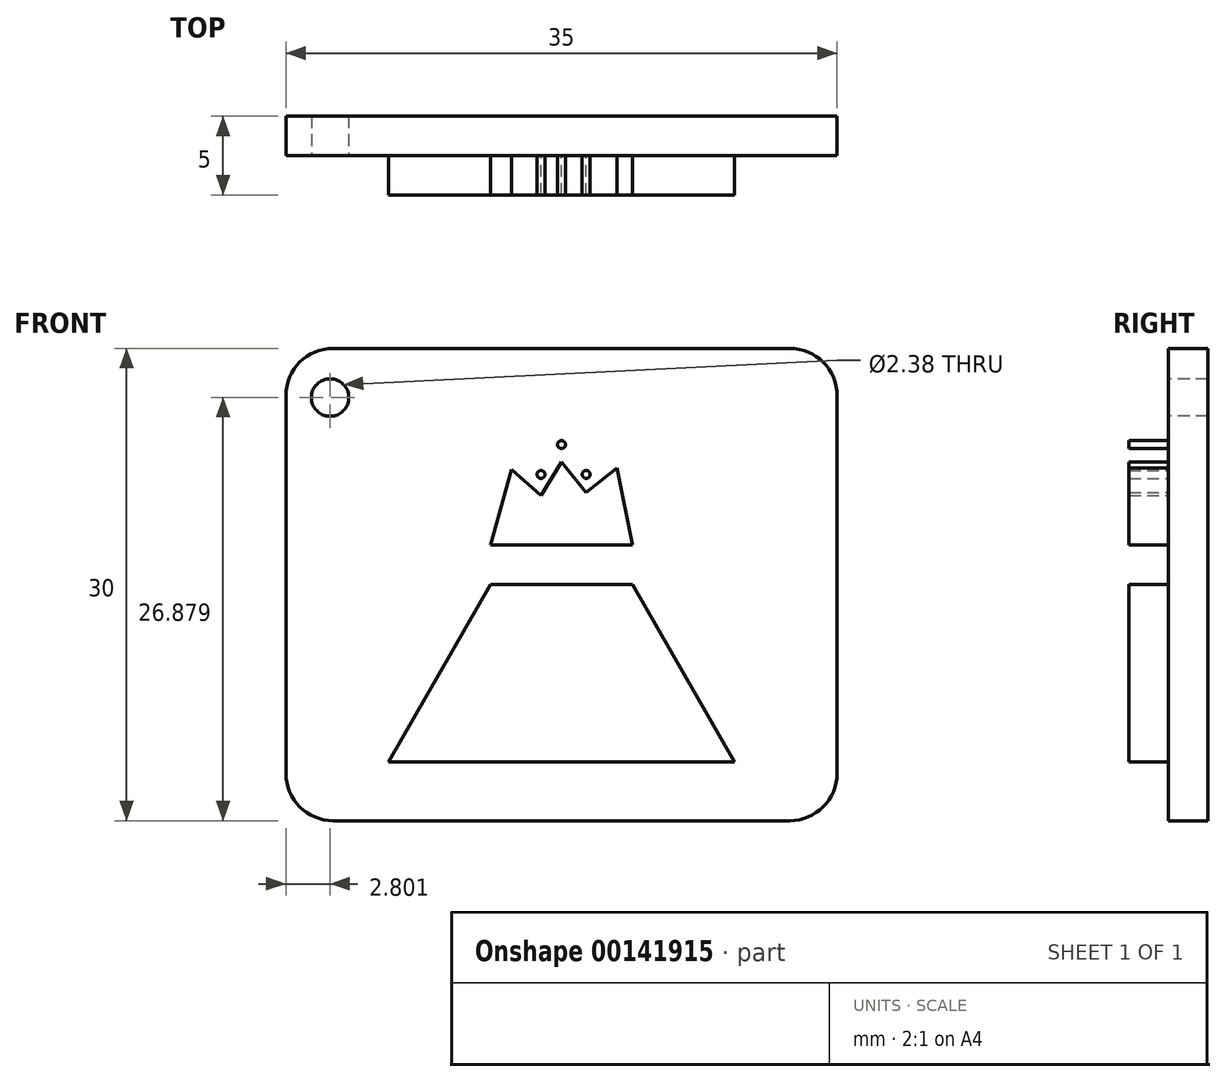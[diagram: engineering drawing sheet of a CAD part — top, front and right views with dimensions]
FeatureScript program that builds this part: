
annotation { "Feature Type Name" : "Feature", "Feature Type Description" : "" }
export const myFeature = defineFeature(function(context is Context, id is Id, definition is map)
    precondition{}
    {
        {
            var Q0;
            Q0=qCreatedBy(makeId("Front.planeOp"),FACE);
            var sketch = newSketch(context, id + "F0", { "sketchPlane" : qUnion([Q0])});
            skLineSegment(sketch, "E0.bottom", {"start": v(17.5, -15) * mm, "end": v(-17.5, -15) * mm});
            skLineSegment(sketch, "E0.top", {"start": v(17.5, 15) * mm, "end": v(-17.5, 15) * mm});
            skLineSegment(sketch, "E0.left", {"start": v(17.5, -15) * mm, "end": v(17.5, 15) * mm});
            skLineSegment(sketch, "E0.right", {"start": v(-17.5, -15) * mm, "end": v(-17.5, 15) * mm});
            skPoint(sketch, "E0.middle", {"position": v(0, 0) * mm});
            skCircle(sketch, "E1", {"center": v(-14.7, 11.88) * mm, "radius": 1.19 * mm});
            skSolve(sketch);
        }
        {
            var Q0;
            Q0 = qSketchRegion(id + "F0", true);
            extrude(context, id + "F1", {"entities" : qUnion([Q0]), "oppositeDirection" : true, "depth" : 2.5 * mm});
        }
        {
            var Q0;
            Q0=qCreatedBy(makeId("Front.planeOp"),FACE);
            var sketch = newSketch(context, id + "F2", { "sketchPlane" : qUnion([Q0])});
            skLineSegment(sketch, "E2", {"start": v(-11, -11.26) * mm, "end": v(11, -11.26) * mm});
            skLineSegment(sketch, "E3", {"start": v(0, -11.26) * mm, "end": v(0, 0) * mm, "construction": true});
            skLineSegment(sketch, "E4", {"start": v(4.5, 0) * mm, "end": v(-4.5, 0) * mm});
            skLineSegment(sketch, "E5", {"start": v(-4.5, 0) * mm, "end": v(-11, -11.26) * mm});
            skLineSegment(sketch, "E6", {"start": v(4.5, 0) * mm, "end": v(11, -11.26) * mm});
            skLineSegment(sketch, "E7", {"start": v(0, 0) * mm, "end": v(0, 2.5) * mm, "construction": true});
            skLineSegment(sketch, "E8", {"start": v(4.5, 2.5) * mm, "end": v(-4.5, 2.5) * mm});
            skLineSegment(sketch, "E9", {"start": v(-4.5, 2.5) * mm, "end": v(-3.16, 7.32) * mm});
            skLineSegment(sketch, "E10", {"start": v(4.5, 2.5) * mm, "end": v(3.52, 7.4) * mm});
            skLineSegment(sketch, "E11", {"start": v(3.52, 7.4) * mm, "end": v(1.57, 5.83) * mm});
            skLineSegment(sketch, "E12", {"start": v(1.57, 5.83) * mm, "end": v(0, 7.78) * mm});
            skLineSegment(sketch, "E13", {"start": v(0, 7.78) * mm, "end": v(-1.3, 5.65) * mm});
            skLineSegment(sketch, "E14", {"start": v(-1.3, 5.65) * mm, "end": v(-3.16, 7.32) * mm});
            skPoint(sketch, "E15", {"position": v(-7.75, -5.63) * mm});
            skPoint(sketch, "E16.endSnap0", {"position": v(0.78, 6.8) * mm});
            skLineSegment(sketch, "E17", {"start": v(-1.3, 5.65) * mm, "end": v(-1.3, 7) * mm, "construction": true});
            skLineSegment(sketch, "E18", {"start": v(1.57, 5.83) * mm, "end": v(1.57, 7) * mm, "construction": true});
            skLineSegment(sketch, "E19", {"start": v(1.57, 7) * mm, "end": v(-1.3, 7) * mm, "construction": true});
            skLineSegment(sketch, "E20", {"start": v(0, 7.78) * mm, "end": v(0, 8.89) * mm, "construction": true});
            skCircle(sketch, "E21", {"center": v(0, 8.89) * mm, "radius": 0.25 * mm});
            skCircle(sketch, "E22", {"center": v(-1.3, 7) * mm, "radius": 0.25 * mm});
            skCircle(sketch, "E23", {"center": v(1.57, 7) * mm, "radius": 0.25 * mm});
            skSolve(sketch);
        }
        {
            var Q0;
            Q0 = qSketchRegion(id + "F2", true);
            extrude(context, id + "F3", {"entities" : qUnion([Q0]), "depth" : 2.5 * mm});
        }
        {
            var Q0;
            Q0=makeQuery(id+"F1.opExtrude","SWEPT_EDGE",EDGE,{"disambiguationData":[OSD([sQuery(id+"F0.wireOp",EDGE,"E0.top"),sQuery(id+"F0.wireOp",EDGE,"E0.left")])]});
            var Q1;
            Q1=makeQuery(id+"F1.opExtrude","SWEPT_EDGE",EDGE,{"disambiguationData":[OSD([sQuery(id+"F0.wireOp",EDGE,"E0.top"),sQuery(id+"F0.wireOp",EDGE,"E0.right")])]});
            var Q2;
            Q2=makeQuery(id+"F1.opExtrude","SWEPT_EDGE",EDGE,{"disambiguationData":[OSD([sQuery(id+"F0.wireOp",EDGE,"E0.bottom"),sQuery(id+"F0.wireOp",EDGE,"E0.right")])]});
            var Q3;
            Q3=makeQuery(id+"F1.opExtrude","SWEPT_EDGE",EDGE,{"disambiguationData":[OSD([sQuery(id+"F0.wireOp",EDGE,"E0.bottom"),sQuery(id+"F0.wireOp",EDGE,"E0.left")])]});
            fillet(context, id + "F4", {"entities" : qUnion([Q0, Q1, Q2, Q3]), "radius" : 3 * mm, "tangentPropagation" : true, "allowEdgeOverflow" : false});
        }
    });
